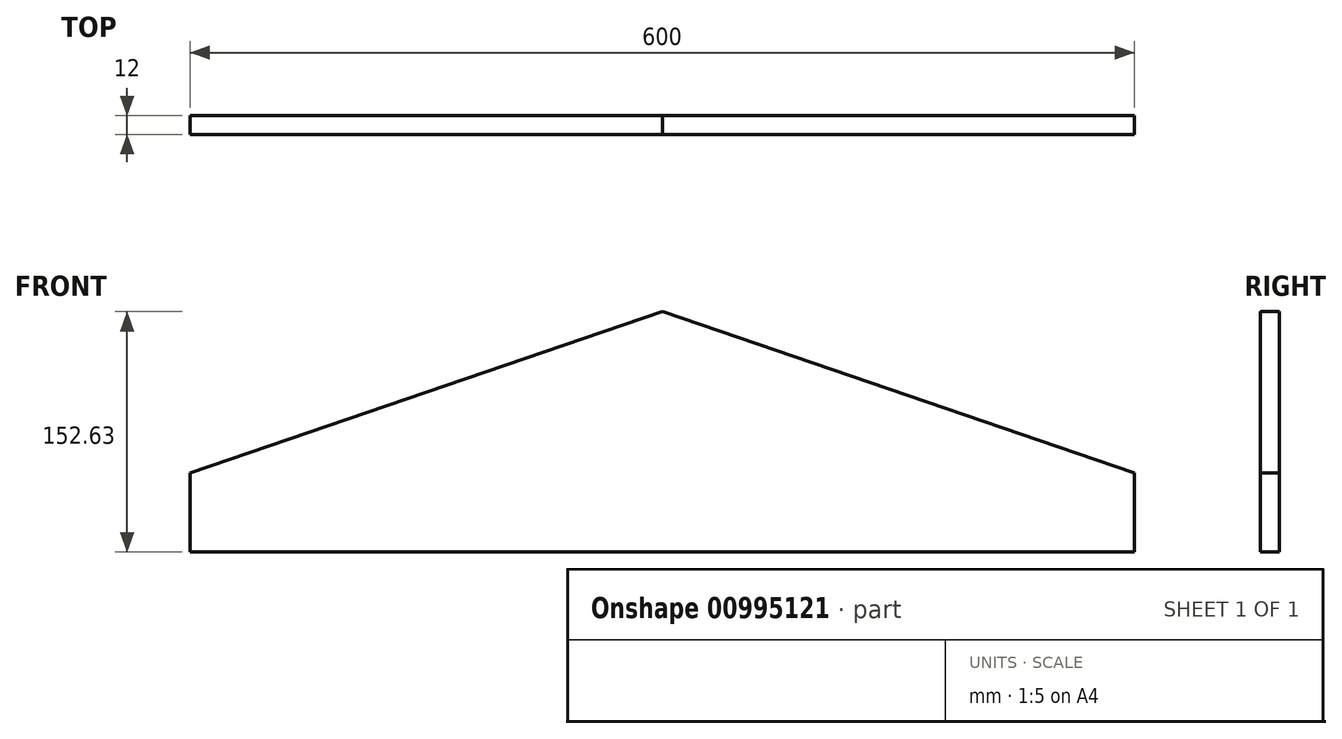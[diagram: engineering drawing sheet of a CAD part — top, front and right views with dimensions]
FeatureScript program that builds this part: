
annotation { "Feature Type Name" : "Feature", "Feature Type Description" : "" }
export const myFeature = defineFeature(function(context is Context, id is Id, definition is map)
    precondition{}
    {
        {
            var Q0;
            Q0=qCreatedBy(makeId("Front.planeOp"),FACE);
            var sketch = newSketch(context, id + "F0", { "sketchPlane" : qUnion([Q0])});
            skLineSegment(sketch, "E0", {"start": v(-380, 0) * mm, "end": v(-380, 350) * mm, "construction": true});
            skLineSegment(sketch, "E1", {"start": v(-380, 350) * mm, "end": v(-300, 377.37) * mm, "construction": true});
            skLineSegment(sketch, "E2", {"start": v(0, 480) * mm, "end": v(300, 377.37) * mm});
            skLineSegment(sketch, "E3", {"start": v(380, 350) * mm, "end": v(380, 0) * mm, "construction": true});
            skLineSegment(sketch, "E4", {"start": v(380, 0) * mm, "end": v(-380, 0) * mm, "construction": true});
            skLineSegment(sketch, "E5", {"start": v(-300, 377.37) * mm, "end": v(-300, 327.37) * mm});
            skLineSegment(sketch, "E6", {"start": v(-300, 327.37) * mm, "end": v(300, 327.37) * mm});
            skLineSegment(sketch, "E7", {"start": v(300, 327.37) * mm, "end": v(300, 377.37) * mm});
            skLineSegment(sketch, "E8", {"start": v(-300, 377.37) * mm, "end": v(0, 480) * mm});
            skLineSegment(sketch, "E9", {"start": v(300, 377.37) * mm, "end": v(380, 350) * mm, "construction": true});
            skSolve(sketch);
        }
        {
            var Q0;
            Q0=qSketchRegion(id+"F0",true);
            extrude(context, id + "F1", {"entities" : qUnion([Q0]), "depth" : 12 * mm, "offsetDistance" : 25 * mm});
        }
    });
